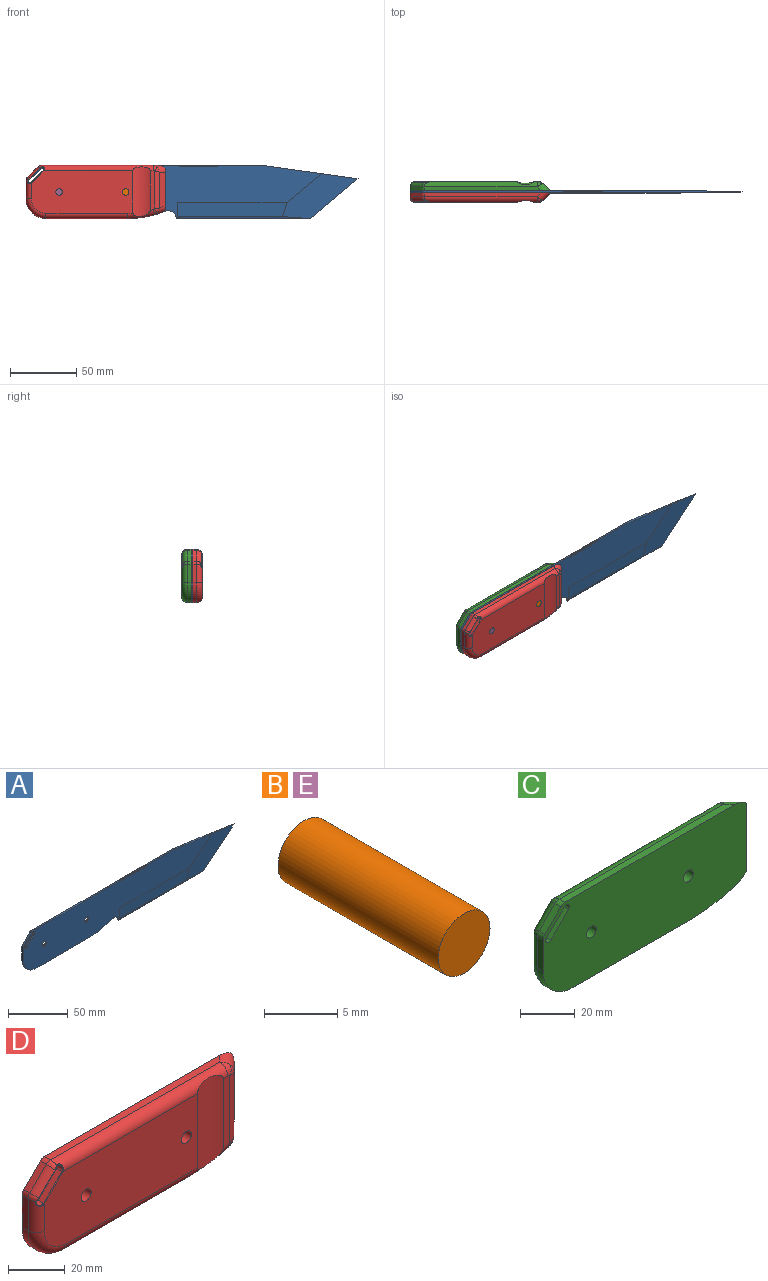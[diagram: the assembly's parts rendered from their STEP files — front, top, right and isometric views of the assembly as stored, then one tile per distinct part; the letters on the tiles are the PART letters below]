
ASSEMBLY  parts=5 mates=6
PART A: 215 faces, bbox 250x19.1x40 mm
  f0: plane 1.5x1mm, normal (0,0,-1), area 1.5mm2, adj f16,f17,f22,f23,f25
  f1: plane 1.5x0.59mm, normal (0,0,1), area 0.8mm2, adj f16,f17,f78,f79,f84,f86,f87,f89
  f2: plane 1.5x0.59mm, normal (0,0,1), area 0.8mm2, adj f16,f17,f87,f88,f93,f95,f96,f98
  f3: plane 1.5x0.59mm, normal (0,0,1), area 0.8mm2, adj f16,f17,f96,f97,f102,f104,f105,f107
  f4: plane 1.5x0.59mm, normal (0,0,1), area 0.8mm2, adj f16,f17,f105,f106,f111,f113,f114,f116
  f5: plane 1.5x0.59mm, normal (0,0,1), area 0.8mm2, adj f16,f17,f114,f115,f120,f122,f123,f125
  f6: plane 1.5x0.59mm, normal (0,0,1), area 0.8mm2, adj f16,f17,f123,f124,f129,f131,f132,f134
  f7: plane 1.5x0.59mm, normal (0,0,1), area 0.8mm2, adj f16,f17,f132,f133,f138,f140,f141,f143
  f8: plane 1.5x0.59mm, normal (0,0,1), area 0.8mm2, adj f16,f17,f141,f142,f147,f149,f150,f152
  f9: plane 1.5x0.59mm, normal (0,0,1), area 0.8mm2, adj f16,f17,f150,f151,f156,f158,f159,f161
  f10: plane 1.5x0.59mm, normal (0,0,1), area 0.8mm2, adj f16,f17,f159,f160,f165,f167,f168,f170
  f11: plane 1.5x0.59mm, normal (0,0,1), area 0.8mm2, adj f16,f17,f168,f169,f174,f176,f177,f179
  f12: plane 1.5x0.59mm, normal (0,0,1), area 0.8mm2, adj f16,f17,f177,f178,f183,f185,f186,f188
  f13: plane 1.5x0.59mm, normal (0,0,1), area 0.8mm2, adj f16,f17,f186,f187,f192,f194,f195,f197
  f14: plane 1.5x0.59mm, normal (0,0,1), area 0.8mm2, adj f16,f17,f195,f196,f201,f203,f204,f206
  f15: plane 103.98x1.5mm, normal (0,0,1), area 155.9mm2, adj f16,f17,f31,f204,f205,f210,f212
  f16: plane 222.55x40mm, normal (0,-1,0), area 6864.1mm2, adj f0,f1,f2,f3,f4,f5,f6,f7
  f17: plane 222.55x40mm, normal (0,1,0), area 6864.1mm2, adj f0,f1,f2,f3,f4,f5,f6,f7
  f18: plane 61.41x1.5mm, normal (0,0,-1), area 92.1mm2, adj f16,f17,f29,f33
  f19: plane 33.36x1.5mm, normal (0,0,1), area 50mm2, adj f16,f17,f21,f78,f80,f85,f86
  f20: plane 13.76x1.5mm, normal (-1,0,0), area 20.6mm2, adj f16,f17,f29,f32
  f21: plane 72x10mm, normal (0.14,0,0.99), area 88.3mm2, adj f16,f17,f19,f27,f28
  f22: cylinder r=6mm len=8.27mm, axis (0,-1,0), area 17.6mm2, adj f0,f16,f17,f33
  f23: plane 12.25x0.75mm, normal (1,0,0), area 1.9mm2, adj f0,f17,f24,f213
  f24: plane 82.68x10.79mm, normal (0,1,-0.02), area 873.5mm2, adj f17,f23,f27,f213
  f25: plane 12.25x0.75mm, normal (1,0,0), area 1.9mm2, adj f0,f16,f26,f214
  f26: plane 82.68x10.79mm, normal (0,-1,-0.02), area 873.5mm2, adj f16,f25,f28,f214
  f27: plane 56.87x33.81mm, normal (0.02,1,-0.03), area 941.4mm2, adj f17,f21,f24,f28,f213
  f28: plane 56.87x33.81mm, normal (0.02,-1,-0.03), area 941.4mm2, adj f16,f21,f26,f27,f214
  f29: cylinder r=15mm len=15mm, axis (0,-1,0), area 35.3mm2, adj f16,f17,f18,f20
  f30: plane 8.24x8.24mm, normal (-0.71,0,0.71), area 17.5mm2, adj f16,f17,f31,f32
  f31: cylinder r=3mm len=2.12mm, axis (0,1,0), area 3.5mm2, adj f15,f16,f17,f30
  f32: cylinder r=3mm len=2.12mm, axis (0,-1,0), area 3.5mm2, adj f16,f17,f20,f30
  f33: cylinder r=75mm len=28.33mm, axis (0,-1,0), area 43.6mm2, adj f16,f17,f18,f22
  f34: plane 9.19x9.19mm, normal (0.71,0,-0.71), area 6.5mm2, adj f36,f37,f41,f43
  f35: plane 9.19x9.19mm, normal (-0.71,0,0.71), area 6.5mm2, adj f36,f37,f38,f44
  f36: cylinder r=1mm len=1.71mm, axis (0,1,0), area 1.6mm2, adj f34,f35,f39,f45
  f37: cylinder r=1mm len=1.71mm, axis (0,1,0), area 1.6mm2, adj f34,f35,f40,f42
  f38: cylinder r=0.5mm len=9.55mm, axis (0.71,0,0.71), area 10.2mm2, adj f17,f35,f39,f40
  f39: torus R=1.5mm, axis (0,-1,0), area 2.9mm2, adj f17,f36,f38,f41
  f40: torus R=1.5mm, axis (0,-1,0), area 2.9mm2, adj f17,f37,f38,f41
  f41: cylinder r=0.5mm len=9.55mm, axis (-0.71,0,-0.71), area 10.2mm2, adj f17,f34,f39,f40
  f42: torus R=1.5mm, axis (0,-1,0), area 2.9mm2, adj f16,f37,f43,f44
  f43: cylinder r=0.5mm len=9.55mm, axis (0.71,0,0.71), area 10.2mm2, adj f16,f34,f42,f45
  f44: cylinder r=0.5mm len=9.55mm, axis (-0.71,0,-0.71), area 10.2mm2, adj f16,f35,f42,f45
  f45: torus R=1.5mm, axis (0,-1,0), area 2.9mm2, adj f16,f36,f43,f44
  f46: cylinder r=2.5mm len=5mm, axis (0,1,0), area 23.6mm2, adj f16,f17
  f47: cylinder r=2.5mm len=5mm, axis (0,1,0), area 23.6mm2, adj f16,f17
  f48: cone r=0.5mm half-angle=3deg, axis (0,1,0), area 0.6mm2, adj f207,f210,f211,f212
  f49: cone r=0.5mm half-angle=3deg, axis (0,-1,0), area 0.6mm2, adj f204,f205,f206,f207
  f50: cone r=0.5mm half-angle=3deg, axis (0,1,0), area 0.6mm2, adj f198,f201,f202,f203
  f51: cone r=0.5mm half-angle=3deg, axis (0,-1,0), area 0.6mm2, adj f195,f196,f197,f198
  f52: cone r=0.5mm half-angle=3deg, axis (0,1,0), area 0.6mm2, adj f189,f192,f193,f194
  f53: cone r=0.5mm half-angle=3deg, axis (0,-1,0), area 0.6mm2, adj f186,f187,f188,f189
  f54: cone r=0.5mm half-angle=3deg, axis (0,1,0), area 0.6mm2, adj f180,f183,f184,f185
  f55: cone r=0.5mm half-angle=3deg, axis (0,-1,0), area 0.6mm2, adj f177,f178,f179,f180
  f56: cone r=0.5mm half-angle=3deg, axis (0,1,0), area 0.6mm2, adj f171,f174,f175,f176
  f57: cone r=0.5mm half-angle=3deg, axis (0,-1,0), area 0.6mm2, adj f168,f169,f170,f171
  f58: cone r=0.5mm half-angle=3deg, axis (0,1,0), area 0.6mm2, adj f162,f165,f166,f167
  f59: cone r=0.5mm half-angle=3deg, axis (0,-1,0), area 0.6mm2, adj f159,f160,f161,f162
  f60: cone r=0.5mm half-angle=3deg, axis (0,1,0), area 0.6mm2, adj f153,f156,f157,f158
  f61: cone r=0.5mm half-angle=3deg, axis (0,-1,0), area 0.6mm2, adj f150,f151,f152,f153
  f62: cone r=0.5mm half-angle=3deg, axis (0,1,0), area 0.6mm2, adj f144,f147,f148,f149
  f63: cone r=0.5mm half-angle=3deg, axis (0,-1,0), area 0.6mm2, adj f141,f142,f143,f144
  f64: cone r=0.5mm half-angle=3deg, axis (0,1,0), area 0.6mm2, adj f135,f138,f139,f140
  f65: cone r=0.5mm half-angle=3deg, axis (0,-1,0), area 0.6mm2, adj f132,f133,f134,f135
  f66: cone r=0.5mm half-angle=3deg, axis (0,1,0), area 0.6mm2, adj f126,f129,f130,f131
  f67: cone r=0.5mm half-angle=3deg, axis (0,-1,0), area 0.6mm2, adj f123,f124,f125,f126
  f68: cone r=0.5mm half-angle=3deg, axis (0,1,0), area 0.6mm2, adj f117,f120,f121,f122
  f69: cone r=0.5mm half-angle=3deg, axis (0,-1,0), area 0.6mm2, adj f114,f115,f116,f117
  f70: cone r=0.5mm half-angle=3deg, axis (0,1,0), area 0.6mm2, adj f108,f111,f112,f113
  f71: cone r=0.5mm half-angle=3deg, axis (0,-1,0), area 0.6mm2, adj f105,f106,f107,f108
  f72: cone r=0.5mm half-angle=3deg, axis (0,1,0), area 0.6mm2, adj f99,f102,f103,f104
  f73: cone r=0.5mm half-angle=3deg, axis (0,-1,0), area 0.6mm2, adj f96,f97,f98,f99
  f74: cone r=0.5mm half-angle=3deg, axis (0,1,0), area 0.6mm2, adj f90,f93,f94,f95
  f75: cone r=0.5mm half-angle=3deg, axis (0,-1,0), area 0.6mm2, adj f87,f88,f89,f90
  f76: cone r=0.5mm half-angle=3deg, axis (0,1,0), area 0.6mm2, adj f81,f84,f85,f86
  f77: cone r=0.5mm half-angle=3deg, axis (0,-1,0), area 0.6mm2, adj f78,f79,f80,f81
  f78: torus R=0.78mm, axis (0,-1,0), area 0.7mm2, adj f1,f16,f19,f77,f79,f80
  f79: bspline ~1.96x0.34mm, area 0.2mm2, adj f1,f77,f78,f82
  f80: bspline ~6.4x0.58mm, area 0.2mm2, adj f19,f77,f78,f83
  f81: torus R=0.75mm, axis (0,1,0), area 0mm2, adj f76,f77,f82,f83
  f82: sphere r=0.25mm, area 0mm2, adj f79,f81,f84
  f83: sphere r=0.25mm, area 0mm2, adj f80,f81,f85
  f84: bspline ~1.96x0.34mm, area 0.2mm2, adj f1,f76,f82,f86
  f85: bspline ~6.4x0.58mm, area 0.2mm2, adj f19,f76,f83,f86
  f86: torus R=0.78mm, axis (0,-1,0), area 0.7mm2, adj f1,f17,f19,f76,f84,f85
  f87: torus R=0.78mm, axis (0,-1,0), area 0.7mm2, adj f1,f2,f16,f75,f88,f89
  f88: bspline ~1.96x0.34mm, area 0.2mm2, adj f2,f75,f87,f91
  f89: bspline ~1.96x0.34mm, area 0.2mm2, adj f1,f75,f87,f92
  f90: torus R=0.75mm, axis (0,1,0), area 0mm2, adj f74,f75,f91,f92
  f91: sphere r=0.25mm, area 0mm2, adj f88,f90,f93
  f92: sphere r=0.25mm, area 0mm2, adj f89,f90,f94
  f93: bspline ~1.96x0.34mm, area 0.2mm2, adj f2,f74,f91,f95
  f94: bspline ~1.96x0.34mm, area 0.2mm2, adj f1,f74,f92,f95
  f95: torus R=0.78mm, axis (0,-1,0), area 0.7mm2, adj f1,f2,f17,f74,f93,f94
  f96: torus R=0.78mm, axis (0,-1,0), area 0.7mm2, adj f2,f3,f16,f73,f97,f98
  f97: bspline ~1.96x0.34mm, area 0.2mm2, adj f3,f73,f96,f100
  f98: bspline ~1.96x0.34mm, area 0.2mm2, adj f2,f73,f96,f101
  f99: torus R=0.75mm, axis (0,1,0), area 0mm2, adj f72,f73,f100,f101
  f100: sphere r=0.25mm, area 0mm2, adj f97,f99,f102
  f101: sphere r=0.25mm, area 0mm2, adj f98,f99,f103
  f102: bspline ~1.96x0.34mm, area 0.2mm2, adj f3,f72,f100,f104
  f103: bspline ~1.96x0.34mm, area 0.2mm2, adj f2,f72,f101,f104
  f104: torus R=0.78mm, axis (0,-1,0), area 0.7mm2, adj f2,f3,f17,f72,f102,f103
  f105: torus R=0.78mm, axis (0,-1,0), area 0.7mm2, adj f3,f4,f16,f71,f106,f107
  f106: bspline ~1.96x0.34mm, area 0.2mm2, adj f4,f71,f105,f109
  f107: bspline ~1.96x0.34mm, area 0.2mm2, adj f3,f71,f105,f110
  f108: torus R=0.75mm, axis (0,1,0), area 0mm2, adj f70,f71,f109,f110
  f109: sphere r=0.25mm, area 0mm2, adj f106,f108,f111
  f110: sphere r=0.25mm, area 0mm2, adj f107,f108,f112
  f111: bspline ~1.96x0.34mm, area 0.2mm2, adj f4,f70,f109,f113
  f112: bspline ~1.96x0.34mm, area 0.2mm2, adj f3,f70,f110,f113
  f113: torus R=0.78mm, axis (0,-1,0), area 0.7mm2, adj f3,f4,f17,f70,f111,f112
  f114: torus R=0.78mm, axis (0,-1,0), area 0.7mm2, adj f4,f5,f16,f69,f115,f116
  f115: bspline ~1.96x0.34mm, area 0.2mm2, adj f5,f69,f114,f118
  f116: bspline ~1.96x0.34mm, area 0.2mm2, adj f4,f69,f114,f119
  f117: torus R=0.75mm, axis (0,1,0), area 0mm2, adj f68,f69,f118,f119
  f118: sphere r=0.25mm, area 0mm2, adj f115,f117,f120
  f119: sphere r=0.25mm, area 0mm2, adj f116,f117,f121
  f120: bspline ~1.96x0.34mm, area 0.2mm2, adj f5,f68,f118,f122
  f121: bspline ~1.96x0.34mm, area 0.2mm2, adj f4,f68,f119,f122
  f122: torus R=0.78mm, axis (0,-1,0), area 0.7mm2, adj f4,f5,f17,f68,f120,f121
  f123: torus R=0.78mm, axis (0,-1,0), area 0.7mm2, adj f5,f6,f16,f67,f124,f125
  f124: bspline ~1.96x0.34mm, area 0.2mm2, adj f6,f67,f123,f127
  f125: bspline ~1.96x0.34mm, area 0.2mm2, adj f5,f67,f123,f128
  f126: torus R=0.75mm, axis (0,1,0), area 0mm2, adj f66,f67,f127,f128
  f127: sphere r=0.25mm, area 0mm2, adj f124,f126,f129
  f128: sphere r=0.25mm, area 0mm2, adj f125,f126,f130
  f129: bspline ~1.96x0.34mm, area 0.2mm2, adj f6,f66,f127,f131
  f130: bspline ~1.96x0.34mm, area 0.2mm2, adj f5,f66,f128,f131
  f131: torus R=0.78mm, axis (0,-1,0), area 0.7mm2, adj f5,f6,f17,f66,f129,f130
  f132: torus R=0.78mm, axis (0,-1,0), area 0.7mm2, adj f6,f7,f16,f65,f133,f134
  f133: bspline ~1.96x0.34mm, area 0.2mm2, adj f7,f65,f132,f136
  f134: bspline ~1.96x0.34mm, area 0.2mm2, adj f6,f65,f132,f137
  f135: torus R=0.75mm, axis (0,1,0), area 0mm2, adj f64,f65,f136,f137
  f136: sphere r=0.25mm, area 0mm2, adj f133,f135,f138
  f137: sphere r=0.25mm, area 0mm2, adj f134,f135,f139
  f138: bspline ~1.96x0.34mm, area 0.2mm2, adj f7,f64,f136,f140
  f139: bspline ~1.96x0.34mm, area 0.2mm2, adj f6,f64,f137,f140
  f140: torus R=0.78mm, axis (0,-1,0), area 0.7mm2, adj f6,f7,f17,f64,f138,f139
  f141: torus R=0.78mm, axis (0,-1,0), area 0.7mm2, adj f7,f8,f16,f63,f142,f143
  f142: bspline ~1.96x0.34mm, area 0.2mm2, adj f8,f63,f141,f145
  f143: bspline ~1.96x0.34mm, area 0.2mm2, adj f7,f63,f141,f146
  f144: torus R=0.75mm, axis (0,1,0), area 0mm2, adj f62,f63,f145,f146
  f145: sphere r=0.25mm, area 0mm2, adj f142,f144,f147
  f146: sphere r=0.25mm, area 0mm2, adj f143,f144,f148
  f147: bspline ~1.96x0.34mm, area 0.2mm2, adj f8,f62,f145,f149
  f148: bspline ~1.96x0.34mm, area 0.2mm2, adj f7,f62,f146,f149
  f149: torus R=0.78mm, axis (0,-1,0), area 0.7mm2, adj f7,f8,f17,f62,f147,f148
  f150: torus R=0.78mm, axis (0,-1,0), area 0.7mm2, adj f8,f9,f16,f61,f151,f152
  f151: bspline ~1.96x0.34mm, area 0.2mm2, adj f9,f61,f150,f154
  f152: bspline ~1.96x0.34mm, area 0.2mm2, adj f8,f61,f150,f155
  f153: torus R=0.75mm, axis (0,1,0), area 0mm2, adj f60,f61,f154,f155
  f154: sphere r=0.25mm, area 0mm2, adj f151,f153,f156
  f155: sphere r=0.25mm, area 0mm2, adj f152,f153,f157
  f156: bspline ~1.96x0.34mm, area 0.2mm2, adj f9,f60,f154,f158
  f157: bspline ~1.96x0.34mm, area 0.2mm2, adj f8,f60,f155,f158
  f158: torus R=0.78mm, axis (0,-1,0), area 0.7mm2, adj f8,f9,f17,f60,f156,f157
  f159: torus R=0.78mm, axis (0,-1,0), area 0.7mm2, adj f9,f10,f16,f59,f160,f161
  f160: bspline ~1.96x0.34mm, area 0.2mm2, adj f10,f59,f159,f163
  f161: bspline ~1.96x0.34mm, area 0.2mm2, adj f9,f59,f159,f164
  f162: torus R=0.75mm, axis (0,1,0), area 0mm2, adj f58,f59,f163,f164
  f163: sphere r=0.25mm, area 0mm2, adj f160,f162,f165
  f164: sphere r=0.25mm, area 0mm2, adj f161,f162,f166
  f165: bspline ~1.96x0.34mm, area 0.2mm2, adj f10,f58,f163,f167
  f166: bspline ~1.96x0.34mm, area 0.2mm2, adj f9,f58,f164,f167
  f167: torus R=0.78mm, axis (0,-1,0), area 0.7mm2, adj f9,f10,f17,f58,f165,f166
  f168: torus R=0.78mm, axis (0,-1,0), area 0.7mm2, adj f10,f11,f16,f57,f169,f170
  f169: bspline ~1.96x0.34mm, area 0.2mm2, adj f11,f57,f168,f172
  f170: bspline ~1.96x0.34mm, area 0.2mm2, adj f10,f57,f168,f173
  f171: torus R=0.75mm, axis (0,1,0), area 0mm2, adj f56,f57,f172,f173
  f172: sphere r=0.25mm, area 0mm2, adj f169,f171,f174
  f173: sphere r=0.25mm, area 0mm2, adj f170,f171,f175
  f174: bspline ~1.96x0.34mm, area 0.2mm2, adj f11,f56,f172,f176
  f175: bspline ~1.96x0.34mm, area 0.2mm2, adj f10,f56,f173,f176
  f176: torus R=0.78mm, axis (0,-1,0), area 0.7mm2, adj f10,f11,f17,f56,f174,f175
  f177: torus R=0.78mm, axis (0,-1,0), area 0.7mm2, adj f11,f12,f16,f55,f178,f179
  f178: bspline ~1.96x0.34mm, area 0.2mm2, adj f12,f55,f177,f181
  f179: bspline ~1.96x0.34mm, area 0.2mm2, adj f11,f55,f177,f182
  f180: torus R=0.75mm, axis (0,1,0), area 0mm2, adj f54,f55,f181,f182
  f181: sphere r=0.25mm, area 0mm2, adj f178,f180,f183
  f182: sphere r=0.25mm, area 0mm2, adj f179,f180,f184
  f183: bspline ~1.96x0.34mm, area 0.2mm2, adj f12,f54,f181,f185
  f184: bspline ~1.96x0.34mm, area 0.2mm2, adj f11,f54,f182,f185
  f185: torus R=0.78mm, axis (0,-1,0), area 0.7mm2, adj f11,f12,f17,f54,f183,f184
  f186: torus R=0.78mm, axis (0,-1,0), area 0.7mm2, adj f12,f13,f16,f53,f187,f188
  f187: bspline ~1.96x0.34mm, area 0.2mm2, adj f13,f53,f186,f190
  f188: bspline ~1.96x0.34mm, area 0.2mm2, adj f12,f53,f186,f191
  f189: torus R=0.75mm, axis (0,1,0), area 0mm2, adj f52,f53,f190,f191
  f190: sphere r=0.25mm, area 0mm2, adj f187,f189,f192
  f191: sphere r=0.25mm, area 0mm2, adj f188,f189,f193
  f192: bspline ~1.96x0.34mm, area 0.2mm2, adj f13,f52,f190,f194
  f193: bspline ~1.96x0.34mm, area 0.2mm2, adj f12,f52,f191,f194
  f194: torus R=0.78mm, axis (0,-1,0), area 0.7mm2, adj f12,f13,f17,f52,f192,f193
  f195: torus R=0.78mm, axis (0,-1,0), area 0.7mm2, adj f13,f14,f16,f51,f196,f197
  f196: bspline ~1.96x0.34mm, area 0.2mm2, adj f14,f51,f195,f199
  f197: bspline ~1.96x0.34mm, area 0.2mm2, adj f13,f51,f195,f200
  f198: torus R=0.75mm, axis (0,1,0), area 0mm2, adj f50,f51,f199,f200
  f199: sphere r=0.25mm, area 0mm2, adj f196,f198,f201
  f200: sphere r=0.25mm, area 0mm2, adj f197,f198,f202
  f201: bspline ~1.96x0.34mm, area 0.2mm2, adj f14,f50,f199,f203
  f202: bspline ~1.96x0.34mm, area 0.2mm2, adj f13,f50,f200,f203
  f203: torus R=0.78mm, axis (0,-1,0), area 0.7mm2, adj f13,f14,f17,f50,f201,f202
  f204: torus R=0.78mm, axis (0,-1,0), area 0.7mm2, adj f14,f15,f16,f49,f205,f206
  f205: bspline ~10.17x0.79mm, area 0.2mm2, adj f15,f49,f204,f208
  f206: bspline ~1.96x0.34mm, area 0.2mm2, adj f14,f49,f204,f209
  f207: torus R=0.75mm, axis (0,1,0), area 0mm2, adj f48,f49,f208,f209
  f208: sphere r=0.25mm, area 0mm2, adj f205,f207,f210
  f209: sphere r=0.25mm, area 0mm2, adj f206,f207,f211
  f210: bspline ~10.17x0.79mm, area 0.2mm2, adj f15,f48,f208,f212
  f211: bspline ~1.96x0.34mm, area 0.2mm2, adj f14,f48,f209,f212
  f212: torus R=0.78mm, axis (0,-1,0), area 0.7mm2, adj f14,f15,f17,f48,f210,f211
  f213: plane 100x1.46mm, normal (0,0.94,-0.34), area 138.7mm2, adj f23,f24,f27,f214
  f214: plane 100x1.46mm, normal (0,-0.94,-0.34), area 138.7mm2, adj f25,f26,f28,f213
PART B: 3 faces, bbox 5x15.5x5 mm
  f0: plane 5x5mm, normal (0,-1,0), area 19.6mm2, adj f1
  f1: cylinder r=2.5mm len=15.5mm, axis (0,1,0), area 243.5mm2, adj f0,f2
  f2: plane 5x5mm, normal (0,1,0), area 19.6mm2, adj f1
PART C: 49 faces, bbox 107.1x10.9x42.3 mm
  f0: plane 29.82x2.79mm, normal (0,1,0), area 82.1mm2, adj f2,f3,f27,f30,f31,f46
  f1: plane 76.14x32.01mm, normal (0,1,0), area 2325.7mm2, adj f2,f3,f15,f16,f21,f23,f25,f34
  f2: cylinder r=4mm len=84.42mm, axis (-1,0,0), area 471.8mm2, adj f0,f1,f4,f20,f31,f36,f48
  f3: torus R=71mm, axis (0,1,0), area 76.9mm2, adj f0,f1,f6,f21,f27,f45
  f4: plane 87.42x3mm, normal (0,0,1), area 257.8mm2, adj f2,f18,f19,f33
  f5: plane 30.84x1.35mm, normal (1,0,0), area 28.9mm2, adj f19,f26,f28,f33
  f6: cylinder r=75mm len=23.85mm, axis (0,-1,0), area 67.8mm2, adj f3,f7,f19,f28
  f7: plane 61.41x3mm, normal (0,0,-1), area 184.2mm2, adj f6,f8,f19,f21
  f8: cylinder r=15mm len=15mm, axis (0,-1,0), area 70.7mm2, adj f7,f9,f19,f23
  f9: plane 13.76x3mm, normal (-1,0,0), area 41.3mm2, adj f8,f10,f19,f25
  f10: cylinder r=3mm len=3mm, axis (0,-1,0), area 7.1mm2, adj f9,f11,f19,f24
  f11: plane 8.24x8.24mm, normal (-0.71,0,0.71), area 35mm2, adj f10,f18,f19,f22
  f12: plane 9.19x9.19mm, normal (-0.71,0,0.71), area 87.7mm2, adj f13,f17,f19,f35
  f13: cylinder r=1.5mm len=6.75mm, axis (0,-1,0), area 28.6mm2, adj f12,f14,f19,f34,f36,f38
  f14: plane 9.2x9.2mm, normal (0.71,0,-0.71), area 78.4mm2, adj f13,f17,f19,f40,f42,f43
  f15: cylinder r=2.5mm len=7mm, axis (0,-1,0), area 110mm2, adj f1,f19
  f16: cylinder r=2.5mm len=7mm, axis (0,-1,0), area 110mm2, adj f1,f19
  f17: cylinder r=1.5mm len=6.75mm, axis (0,-1,0), area 28.6mm2, adj f12,f14,f19,f37,f39,f41
  f18: cylinder r=3mm len=3mm, axis (0,-1,0), area 7.1mm2, adj f4,f11,f19,f20
  f19: plane 105.39x40.66mm, normal (0,-1,0), area 3947.4mm2, adj f4,f5,f6,f7,f8,f9,f10,f11
  f20: bspline ~3.66x2.35mm, area 7.3mm2, adj f2,f18,f22,f38,f40
  f21: cylinder r=4mm len=61.41mm, axis (1,0,0), area 385.8mm2, adj f1,f3,f7,f23
  f22: cylinder r=4mm len=9.41mm, axis (0.71,0,0.71), area 43.4mm2, adj f11,f20,f24,f42
  f23: torus R=11mm, axis (0,1,0), area 133.7mm2, adj f1,f8,f21,f25
  f24: bspline ~3.66x2.35mm, area 7.3mm2, adj f10,f22,f25,f41,f43
  f25: cylinder r=4mm len=13.76mm, axis (0,0,-1), area 78.5mm2, adj f1,f9,f23,f24,f39
  f26: plane 27.01x4.54mm, normal (0.71,0.71,0), area 168.5mm2, adj f5,f28,f30,f33
  f27: bspline ~4.85x4.4mm, area 10mm2, adj f0,f3,f28,f29
  f28: bspline ~9.09x7.84mm, area 42.9mm2, adj f5,f6,f19,f26,f27,f29
  f29: bspline ~4.49x4.27mm, area 5.7mm2, adj f27,f28,f30
  f30: cylinder r=5mm len=28.58mm, axis (0,0,-1), area 109.1mm2, adj f0,f26,f29,f32
  f31: bspline ~4.78x4.51mm, area 12.7mm2, adj f0,f2,f32,f33
  f32: bspline ~4.19x3.97mm, area 5.2mm2, adj f30,f31,f33
  f33: cylinder r=5mm len=9.57mm, axis (0.71,-0.71,0), area 49.5mm2, adj f4,f5,f19,f26,f31,f32
  f34: bspline ~0.31x0.31mm, area 0.1mm2, adj f1,f13,f35,f36
  f35: bspline ~9.37x9.37mm, area 5.3mm2, adj f1,f12,f34,f37
  f36: bspline ~3.04x2.51mm, area 2.5mm2, adj f2,f13,f34,f38
  f37: bspline ~0.31x0.31mm, area 0.1mm2, adj f1,f17,f35,f39
  f38: bspline ~0.84x0.7mm, area 0.4mm2, adj f13,f20,f36,f40
  f39: bspline ~3.07x2.51mm, area 2.5mm2, adj f17,f25,f37,f41
  f40: bspline ~1x0.92mm, area 0.6mm2, adj f14,f20,f38,f42
  f41: bspline ~0.72x0.7mm, area 0.4mm2, adj f17,f24,f39,f43
  f42: bspline ~8.28x8.28mm, area 7.4mm2, adj f14,f22,f40,f43
  f43: bspline ~1x0.92mm, area 0.6mm2, adj f14,f24,f41,f42
  f44: cylinder r=17.5mm len=31.9mm, axis (0,0,-1), area 388.8mm2, adj f45,f46,f47,f48
  f45: bspline ~13.76x5.59mm, area 29.1mm2, adj f3,f44,f46,f47
  f46: cylinder r=2mm len=29.82mm, axis (0,0,-1), area 21.5mm2, adj f0,f44,f45,f48
  f47: cylinder r=2mm len=31.9mm, axis (0,0,-1), area 23mm2, adj f1,f44,f45,f48
  f48: bspline ~13.74x4.06mm, area 27.8mm2, adj f2,f44,f46,f47
PART D: 45 faces, bbox 107.1x10.9x42.3 mm
  f0: plane 29.91x3.17mm, normal (0,-1,0), area 93.3mm2, adj f2,f3,f27,f30,f31,f44
  f1: plane 76.51x32.01mm, normal (0,-1,0), area 2337.7mm2, adj f2,f3,f15,f16,f21,f23,f25,f34
  f2: cylinder r=4mm len=84.42mm, axis (-1,0,0), area 489.4mm2, adj f0,f1,f4,f20,f31,f36,f44
  f3: torus R=71mm, axis (0,-1,0), area 95.3mm2, adj f0,f1,f6,f21,f27,f44
  f4: plane 87.42x3mm, normal (0,0,1), area 257.8mm2, adj f2,f18,f19,f33
  f5: plane 30.84x1.35mm, normal (1,0,0), area 28.9mm2, adj f19,f26,f28,f33
  f6: cylinder r=75mm len=23.85mm, axis (0,1,0), area 67.8mm2, adj f3,f7,f19,f28
  f7: plane 61.41x3mm, normal (0,0,-1), area 184.2mm2, adj f6,f8,f19,f21
  f8: cylinder r=15mm len=15mm, axis (0,1,0), area 70.7mm2, adj f7,f9,f19,f23
  f9: plane 13.76x3mm, normal (-1,0,0), area 41.3mm2, adj f8,f10,f19,f25
  f10: cylinder r=3mm len=3mm, axis (0,1,0), area 7.1mm2, adj f9,f11,f19,f24
  f11: plane 8.24x8.24mm, normal (-0.71,0,0.71), area 35mm2, adj f10,f18,f19,f22
  f12: plane 9.19x9.19mm, normal (-0.71,0,0.71), area 87.7mm2, adj f13,f17,f19,f35
  f13: cylinder r=1.5mm len=6.75mm, axis (0,1,0), area 28.6mm2, adj f12,f14,f19,f34,f36,f38
  f14: plane 9.2x9.2mm, normal (0.71,0,-0.71), area 78.4mm2, adj f13,f17,f19,f40,f42,f43
  f15: cylinder r=2.5mm len=7mm, axis (0,1,0), area 110mm2, adj f1,f19
  f16: cylinder r=2.5mm len=7mm, axis (0,1,0), area 110mm2, adj f1,f19
  f17: cylinder r=1.5mm len=6.75mm, axis (0,1,0), area 28.6mm2, adj f12,f14,f19,f37,f39,f41
  f18: cylinder r=3mm len=3mm, axis (0,1,0), area 7.1mm2, adj f4,f11,f19,f20
  f19: plane 105.39x40.66mm, normal (0,1,0), area 3947.4mm2, adj f4,f5,f6,f7,f8,f9,f10,f11
  f20: bspline ~3.66x2.35mm, area 7.3mm2, adj f2,f18,f22,f38,f40
  f21: cylinder r=4mm len=61.41mm, axis (1,0,0), area 385.8mm2, adj f1,f3,f7,f23
  f22: cylinder r=4mm len=9.41mm, axis (0.71,0,0.71), area 43.4mm2, adj f11,f20,f24,f42
  f23: torus R=11mm, axis (0,-1,0), area 133.7mm2, adj f1,f8,f21,f25
  f24: bspline ~3.66x2.35mm, area 7.3mm2, adj f10,f22,f25,f41,f43
  f25: cylinder r=4mm len=13.76mm, axis (0,0,-1), area 78.5mm2, adj f1,f9,f23,f24,f39
  f26: plane 27.01x4.54mm, normal (0.71,-0.71,0), area 168.5mm2, adj f5,f28,f30,f33
  f27: bspline ~4.85x4.4mm, area 10mm2, adj f0,f3,f28,f29
  f28: bspline ~9.09x7.84mm, area 42.9mm2, adj f5,f6,f19,f26,f27,f29
  f29: bspline ~4.49x4.27mm, area 5.7mm2, adj f27,f28,f30
  f30: cylinder r=5mm len=28.58mm, axis (0,0,-1), area 109.1mm2, adj f0,f26,f29,f32
  f31: bspline ~4.78x4.51mm, area 12.7mm2, adj f0,f2,f32,f33
  f32: bspline ~4.19x3.97mm, area 5.2mm2, adj f30,f31,f33
  f33: cylinder r=5mm len=9.57mm, axis (0.71,0.71,0), area 49.5mm2, adj f4,f5,f19,f26,f31,f32
  f34: bspline ~0.31x0.31mm, area 0.1mm2, adj f1,f13,f35,f36
  f35: bspline ~9.37x9.37mm, area 5.3mm2, adj f1,f12,f34,f37
  f36: bspline ~3.04x2.51mm, area 2.5mm2, adj f2,f13,f34,f38
  f37: bspline ~0.31x0.31mm, area 0.1mm2, adj f1,f17,f35,f39
  f38: bspline ~0.84x0.7mm, area 0.4mm2, adj f13,f20,f36,f40
  f39: bspline ~3.07x2.51mm, area 2.5mm2, adj f17,f25,f37,f41
  f40: bspline ~1x0.92mm, area 0.6mm2, adj f14,f20,f38,f42
  f41: bspline ~0.84x0.7mm, area 0.4mm2, adj f17,f24,f39,f43
  f42: bspline ~8.28x8.28mm, area 7.4mm2, adj f14,f22,f40,f43
  f43: bspline ~1x0.92mm, area 0.6mm2, adj f14,f24,f41,f42
  f44: cylinder r=17.5mm len=31.88mm, axis (0,0,-1), area 411.2mm2, adj f0,f1,f2,f3
PART E: same geometry as B
PLACE A at identity fixed
PLACE B at identity
PLACE C at identity
PLACE D at identity
PLACE E t=(-50,0,0)mm
MATE cylindrical D.f15 <-> B.f1  axis (0,-1,0) through (75,-7.75,20)mm
MATE planar A.f17 <-> C.f19  axis (0,1,0) through (96.81,0.75,22.46)mm
MATE cylindrical C.f16 <-> A.f46  axis (0,1,0) through (25,7.75,20)mm
MATE planar B.f1 <-> D.f1  axis (0,1,0) through (75,-7.75,20)mm
MATE cylindrical A.f47 <-> B.f1  axis (0,-1,0) through (75,-0.75,20)mm
MATE cylindrical E.f1 <-> A.f46  axis (0,1,0) through (25,-7.75,20)mm
